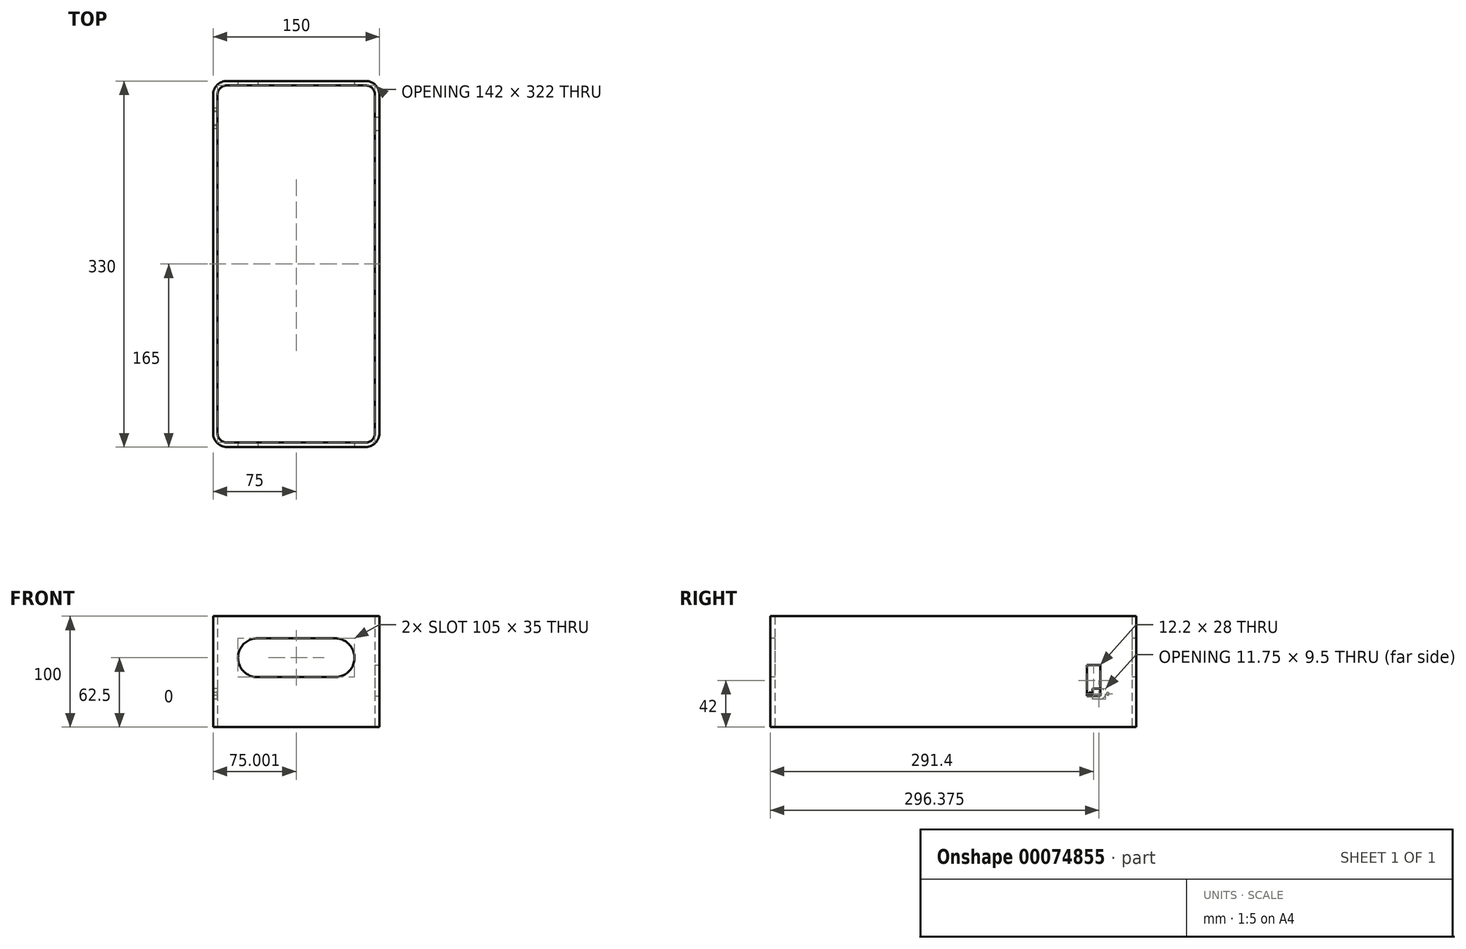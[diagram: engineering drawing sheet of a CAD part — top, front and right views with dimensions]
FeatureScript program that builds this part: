
annotation { "Feature Type Name" : "Feature", "Feature Type Description" : "" }
export const myFeature = defineFeature(function(context is Context, id is Id, definition is map)
    precondition{}
    {
        {
            var Q0;
            Q0=qCreatedBy(makeId("Top.planeOp"),FACE);
            var sketch = newSketch(context, id + "F0", { "sketchPlane" : qUnion([Q0])});
            skLineSegment(sketch, "E0.bottom", {"start": v(12.5, 0) * mm, "end": v(137.5, 0) * mm});
            skLineSegment(sketch, "E0.top", {"start": v(12.5, 330) * mm, "end": v(137.5, 330) * mm});
            skLineSegment(sketch, "E0.left", {"start": v(0, 12.5) * mm, "end": v(0, 317.5) * mm});
            skLineSegment(sketch, "E0.right", {"start": v(150, 12.5) * mm, "end": v(150, 317.5) * mm});
            skPoint(sketch, "E1.visualSharp", {"position": v(0, 330) * mm});
            skArc(sketch, "E1.filletArc", {"start": v(12.5, 330) * mm, "mid": v(3.66, 326.34) * mm, "end": v(0, 317.5) * mm});
            skPoint(sketch, "E2.visualSharp", {"position": v(0, 0) * mm});
            skArc(sketch, "E2.filletArc", {"start": v(0, 12.5) * mm, "mid": v(3.66, 3.66) * mm, "end": v(12.5, 0) * mm});
            skPoint(sketch, "E3.visualSharp", {"position": v(150, 0) * mm});
            skArc(sketch, "E3.filletArc", {"start": v(137.5, 0) * mm, "mid": v(146.34, 3.66) * mm, "end": v(150, 12.5) * mm});
            skPoint(sketch, "E4.visualSharp", {"position": v(150, 330) * mm});
            skArc(sketch, "E4.filletArc", {"start": v(150, 317.5) * mm, "mid": v(146.34, 326.34) * mm, "end": v(137.5, 330) * mm});
            skLineSegment(sketch, "E5.0", {"start": v(4, 12.5) * mm, "end": v(4, 317.5) * mm});
            skLineSegment(sketch, "E6.0", {"start": v(12.5, 326) * mm, "end": v(137.5, 326) * mm});
            skArc(sketch, "E7.0", {"start": v(12.5, 326) * mm, "mid": v(6.49, 323.51) * mm, "end": v(4, 317.5) * mm});
            skLineSegment(sketch, "E8.0", {"start": v(146, 12.5) * mm, "end": v(146, 317.5) * mm});
            skArc(sketch, "E9.0", {"start": v(146, 317.5) * mm, "mid": v(143.51, 323.51) * mm, "end": v(137.5, 326) * mm});
            skArc(sketch, "E10.0", {"start": v(137.5, 4) * mm, "mid": v(143.51, 6.49) * mm, "end": v(146, 12.5) * mm});
            skLineSegment(sketch, "E11.0", {"start": v(12.5, 4) * mm, "end": v(137.5, 4) * mm});
            skArc(sketch, "E12.0", {"start": v(4, 12.5) * mm, "mid": v(6.49, 6.49) * mm, "end": v(12.5, 4) * mm});
            skSolve(sketch);
        }
        {
            var Q0;
            Q0=makeQuery(id+"F0.imprint","IMPRINT",FACE,{"disambiguationData":[TD([[makeQuery(id+"F0.imprint","IMPRINT",EDGE,{"derivedFrom":sQuery(id+"F0.wireOp",EDGE,"E0.bottom")}),1.0]])]});
            extrude(context, id + "F1", {"entities" : qUnion([Q0]), "depth" : 100 * mm});
        }
        {
            var Q0;
            Q0=makeQuery(id+"F1.opExtrude","SWEPT_FACE",FACE,{"disambiguationData":[OSD([sQuery(id+"F0.wireOp",EDGE,"E0.bottom")])]});
            var sketch = newSketch(context, id + "F2", { "sketchPlane" : qUnion([Q0])});
            skLineSegment(sketch, "E13.0", {"start": v(7.5, -5) * mm, "end": v(142.5, -5) * mm, "construction": true});
            skLineSegment(sketch, "E13.1", {"start": v(7.5, 105) * mm, "end": v(7.5, -5) * mm, "construction": true});
            skLineSegment(sketch, "E13.2", {"start": v(142.5, 105) * mm, "end": v(7.5, 105) * mm, "construction": true});
            skLineSegment(sketch, "E13.3", {"start": v(142.5, -5) * mm, "end": v(142.5, 105) * mm, "construction": true});
            skArc(sketch, "E14", {"start": v(40, 80) * mm, "mid": v(22.5, 62.33) * mm, "end": v(40.35, 45) * mm});
            skArc(sketch, "E15", {"start": v(110, 45) * mm, "mid": v(127.5, 62.52) * mm, "end": v(109.96, 80) * mm});
            skLineSegment(sketch, "E16", {"start": v(40.35, 45) * mm, "end": v(110, 45) * mm});
            skLineSegment(sketch, "E17", {"start": v(40, 80) * mm, "end": v(110, 80) * mm});
            skSolve(sketch);
        }
        {
            var Q0;
            {var subQ0=sQuery(id+"F2.wireOp",EDGE,"E14");Q0=makeQuery(id+"F2.imprint","IMPRINT",FACE,{"disambiguationData":[TD([[makeQuery(id+"F2.imprint","IMPRINT",EDGE,{"derivedFrom":subQ0}),1.0]])]});}
            extrude(context, id + "F3", {"entities" : qUnion([Q0]), "operationType" : NewBodyOperationType.REMOVE, "endBound" : BoundingType.THROUGH_ALL, "oppositeDirection" : true, "depth" : 25 * mm});
        }
        {
            var Q0;
            Q0=makeQuery(id+"F1.opExtrude","SWEPT_FACE",FACE,{"disambiguationData":[OSD([sQuery(id+"F0.wireOp",EDGE,"E0.right")])]});
            var sketch = newSketch(context, id + "F4", { "sketchPlane" : qUnion([Q0])});
            skLineSegment(sketch, "E18.0", {"start": v(297.5, 44) * mm, "end": v(297.5, 0) * mm, "construction": true});
            skLineSegment(sketch, "E19.bottom", {"start": v(297.5, 22) * mm, "end": v(285.3, 22) * mm});
            skLineSegment(sketch, "E19.top", {"start": v(297.5, 50) * mm, "end": v(285.3, 50) * mm});
            skLineSegment(sketch, "E19.left", {"start": v(297.5, 22) * mm, "end": v(297.5, 50) * mm});
            skLineSegment(sketch, "E19.right", {"start": v(285.3, 22) * mm, "end": v(285.3, 50) * mm});
            skSolve(sketch);
        }
        {
            var Q0;
            Q0=makeQuery(id+"F4.imprint","IMPRINT",FACE,{"disambiguationData":[TD([[makeQuery(id+"F4.imprint","IMPRINT",EDGE,{"derivedFrom":sQuery(id+"F4.wireOp",EDGE,"E19.bottom")}),-1.0]])]});
            extrude(context, id + "F5", {"entities" : qUnion([Q0]), "operationType" : NewBodyOperationType.REMOVE, "oppositeDirection" : true, "depth" : 25 * mm});
        }
        {
            var Q0;
            Q0=makeQuery(id+"F5.boolean.opBoolean","COPY",FACE,{"derivedFrom":makeQuery(id+"F5.opExtrude","SWEPT_FACE",FACE,{"disambiguationData":[OSD([sQuery(id+"F4.wireOp",EDGE,"E19.bottom")])]})});
            extrude(context, id + "F6", {"entities" : qUnion([Q0]), "operationType" : NewBodyOperationType.ADD, "depth" : 6 * mm});
        }
        {
            var Q0;
            Q0=makeQuery(id+"F5.boolean.opBoolean","COPY",FACE,{"derivedFrom":makeQuery(id+"F5.opExtrude","SWEPT_FACE",FACE,{"disambiguationData":[OSD([sQuery(id+"F4.wireOp",EDGE,"E19.top")])]})});
            extrude(context, id + "F7", {"entities" : qUnion([Q0]), "operationType" : NewBodyOperationType.REMOVE, "oppositeDirection" : true, "depth" : 6 * mm});
        }
        {
            var Q0;
            Q0=makeQuery(id+"F1.opExtrude","SWEPT_FACE",FACE,{"disambiguationData":[OSD([sQuery(id+"F0.wireOp",EDGE,"E0.left")])]});
            var sketch = newSketch(context, id + "F8", { "sketchPlane" : qUnion([Q0])});
            skArc(sketch, "E20", {"start": v(-297.5, 34.75) * mm, "mid": v(-302.25, 30) * mm, "end": v(-297.5, 25.25) * mm});
            skLineSegment(sketch, "E21.0", {"start": v(-290.5, 34.75) * mm, "end": v(-290.5, 25.25) * mm});
            skLineSegment(sketch, "E22", {"start": v(-297.5, 34.75) * mm, "end": v(-290.5, 34.75) * mm});
            skLineSegment(sketch, "E23", {"start": v(-297.5, 25.25) * mm, "end": v(-290.5, 25.25) * mm});
            skCircle(sketch, "E24", {"center": v(-304.25, 30) * mm, "radius": 1.25 * mm});
            skCircle(sketch, "E25", {"center": v(-288.35, 30) * mm, "radius": 1.25 * mm});
            skSolve(sketch);
        }
        {
            var Q0;
            Q0=makeQuery(id+"F8.imprint","IMPRINT",FACE,{"disambiguationData":[TD([[makeQuery(id+"F8.imprint","IMPRINT",EDGE,{"derivedFrom":sQuery(id+"F8.wireOp",EDGE,"E20")}),1.0]])]});
            extrude(context, id + "F9", {"entities" : qUnion([Q0]), "operationType" : NewBodyOperationType.REMOVE, "endBound" : BoundingType.UP_TO_NEXT, "oppositeDirection" : true, "depth" : 25 * mm});
        }
        {
            var Q0;
            Q0 = qSketchRegion(id + "F8", true);
            extrude(context, id + "F10", {"entities" : qUnion([Q0]), "operationType" : NewBodyOperationType.REMOVE, "oppositeDirection" : true, "depth" : 25 * mm});
        }
    });
